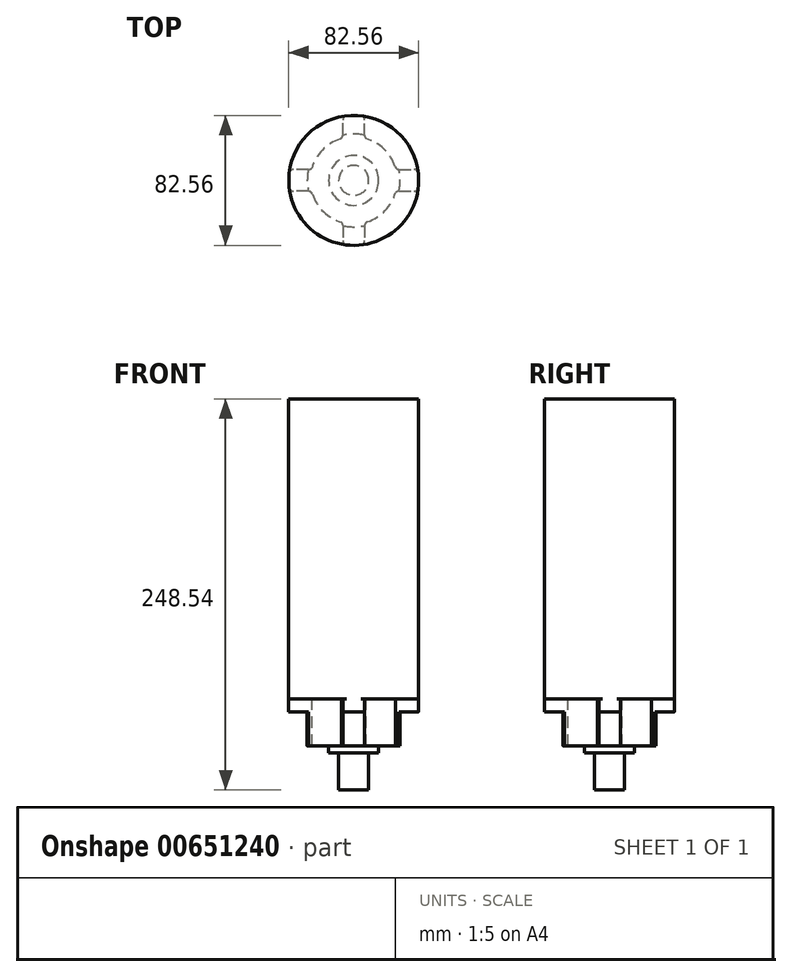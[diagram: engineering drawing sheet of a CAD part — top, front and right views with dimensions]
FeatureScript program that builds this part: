
annotation { "Feature Type Name" : "Feature", "Feature Type Description" : "" }
export const myFeature = defineFeature(function(context is Context, id is Id, definition is map)
    precondition{}
    {
        {
            var Q0;
            Q0=qCreatedBy(makeId("Top.planeOp"),FACE);
            var sketch = newSketch(context, id + "F0", { "sketchPlane" : qUnion([Q0])});
            skCircle(sketch, "E0", {"center": v(0, 0) * mm, "radius": 41.28 * mm});
            skSolve(sketch);
        }
        {
            var Q0;
            Q0=makeQuery(id+"F0.imprint","IMPRINT",FACE,{"disambiguationData":[TD([[makeQuery(id+"F0.imprint","IMPRINT",EDGE,{"derivedFrom":sQuery(id+"F0.wireOp",EDGE,"E0")}),1.0]])]});
            extrude(context, id + "F1", {"entities" : qUnion([Q0]), "depth" : 190.5 * mm, "offsetDistance" : 25.4 * mm});
        }
        {
            var Q0;
            Q0=makeQuery(id+"F1.opExtrude","CAP_FACE",FACE,{"disambiguationData":[OSD([sQuery(id+"F0.wireOp",EDGE,"E0")])],"isStart":true});
            var sketch = newSketch(context, id + "F2", { "sketchPlane" : qUnion([Q0])});
            skLineSegment(sketch, "E1", {"start": v(0, 0) * mm, "end": v(0, 8.34) * mm});
            skLineSegment(sketch, "E2", {"start": v(0, 0) * mm, "end": v(6.98, 0) * mm});
            skLineSegment(sketch, "E3", {"start": v(6.91, 28.9) * mm, "end": v(6.91, 38.32) * mm});
            skLineSegment(sketch, "E4.MirrorCS", {"start": v(-6.91, 28.68) * mm, "end": v(-6.91, 38.32) * mm});
            skLineSegment(sketch, "E5.MirrorCS", {"start": v(-6.91, 28.68) * mm, "end": v(-6.91, 28.65) * mm});
            skArc(sketch, "E6", {"start": v(-11.65, 39.6) * mm, "mid": v(-0.46, -41.27) * mm, "end": v(12.53, 39.33) * mm});
            skArc(sketch, "E7", {"start": v(4.48, 41.03) * mm, "mid": v(0, 41.27) * mm, "end": v(-4.48, 41.03) * mm});
            skPoint(sketch, "E8.newPointB", {"position": v(6.91, 40.69) * mm});
            skArc(sketch, "E8.filletArc", {"start": v(6.91, 38.32) * mm, "mid": v(6.22, 40.14) * mm, "end": v(4.48, 41.03) * mm});
            skPoint(sketch, "E9.newPointB", {"position": v(-6.91, 40.69) * mm});
            skArc(sketch, "E9.filletArc", {"start": v(-4.48, 41.03) * mm, "mid": v(-6.22, 40.14) * mm, "end": v(-6.91, 38.32) * mm});
            skPoint(sketch, "E10.newPointA", {"position": v(6.91, 28.65) * mm});
            skArc(sketch, "E10.filletArc", {"start": v(6.91, 28.9) * mm, "mid": v(7.43, 27.3) * mm, "end": v(8.8, 26.3) * mm});
            skPoint(sketch, "E11.MirrorP", {"position": v(-6.91, 28.65) * mm});
            skArc(sketch, "E12.MirrorCS", {"start": v(-6.91, 28.68) * mm, "mid": v(-7.17, 27.52) * mm, "end": v(-7.9, 26.57) * mm});
            skLineSegment(sketch, "E13.1.0", {"start": v(-28.68, -6.91) * mm, "end": v(-38.32, -6.91) * mm});
            skArc(sketch, "E13.1.1", {"start": v(-41.03, -4.48) * mm, "mid": v(-40.14, -6.22) * mm, "end": v(-38.32, -6.91) * mm});
            skArc(sketch, "E13.1.2", {"start": v(-38.32, 6.91) * mm, "mid": v(-40.14, 6.22) * mm, "end": v(-41.03, 4.48) * mm});
            skLineSegment(sketch, "E13.1.3", {"start": v(-28.9, 6.91) * mm, "end": v(-38.32, 6.91) * mm});
            skArc(sketch, "E13.1.4", {"start": v(-28.9, 6.91) * mm, "mid": v(-27.3, 7.43) * mm, "end": v(-26.3, 8.8) * mm});
            skArc(sketch, "E13.1.5", {"start": v(-28.68, -6.91) * mm, "mid": v(-27.52, -7.17) * mm, "end": v(-26.57, -7.9) * mm});
            skLineSegment(sketch, "E13.2.0", {"start": v(6.91, -28.68) * mm, "end": v(6.91, -38.32) * mm});
            skArc(sketch, "E13.2.1", {"start": v(4.48, -41.03) * mm, "mid": v(6.22, -40.14) * mm, "end": v(6.91, -38.32) * mm});
            skArc(sketch, "E13.2.2", {"start": v(-6.91, -38.32) * mm, "mid": v(-6.22, -40.14) * mm, "end": v(-4.48, -41.03) * mm});
            skLineSegment(sketch, "E13.2.3", {"start": v(-6.91, -28.9) * mm, "end": v(-6.91, -38.32) * mm});
            skArc(sketch, "E13.2.4", {"start": v(-6.91, -28.9) * mm, "mid": v(-7.43, -27.3) * mm, "end": v(-8.8, -26.3) * mm});
            skArc(sketch, "E13.2.5", {"start": v(6.91, -28.68) * mm, "mid": v(7.17, -27.52) * mm, "end": v(7.9, -26.57) * mm});
            skLineSegment(sketch, "E13.3.0", {"start": v(28.68, 6.91) * mm, "end": v(38.32, 6.91) * mm});
            skArc(sketch, "E13.3.1", {"start": v(41.03, 4.48) * mm, "mid": v(40.14, 6.22) * mm, "end": v(38.32, 6.91) * mm});
            skArc(sketch, "E13.3.2", {"start": v(38.32, -6.91) * mm, "mid": v(40.14, -6.22) * mm, "end": v(41.03, -4.48) * mm});
            skLineSegment(sketch, "E13.3.3", {"start": v(28.9, -6.91) * mm, "end": v(38.32, -6.91) * mm});
            skArc(sketch, "E13.3.4", {"start": v(28.9, -6.91) * mm, "mid": v(27.3, -7.43) * mm, "end": v(26.3, -8.8) * mm});
            skArc(sketch, "E13.3.5", {"start": v(28.68, 6.91) * mm, "mid": v(27.52, 7.17) * mm, "end": v(26.57, 7.9) * mm});
            skArc(sketch, "E14", {"start": v(-26.57, -7.9) * mm, "mid": v(-19.93, -19.27) * mm, "end": v(-8.8, -26.3) * mm});
            skArc(sketch, "E15.1.0", {"start": v(7.9, -26.57) * mm, "mid": v(19.27, -19.93) * mm, "end": v(26.3, -8.8) * mm});
            skArc(sketch, "E15.2.0", {"start": v(26.57, 7.9) * mm, "mid": v(19.93, 19.27) * mm, "end": v(8.8, 26.3) * mm});
            skArc(sketch, "E16.3.3.0", {"start": v(-7.9, 26.57) * mm, "mid": v(-19.27, 19.93) * mm, "end": v(-26.3, 8.8) * mm});
            skSolve(sketch);
        }
        {
            var Q0;
            Q0=makeQuery(id+"F2.imprint","IMPRINT",FACE,{"disambiguationData":[TD([[makeQuery(id+"F2.imprint","IMPRINT",EDGE,{"derivedFrom":sQuery(id+"F2.wireOp",EDGE,"E3")}),1.0]])]});
            extrude(context, id + "F3", {"entities" : qUnion([Q0]), "operationType" : NewBodyOperationType.ADD, "depth" : 8.25 * mm, "offsetDistance" : 25.4 * mm});
        }
        {
            var Q0;
            Q0=makeQuery(id+"F3.opExtrude","CAP_FACE",FACE,{"disambiguationData":[OSD([sQuery(id+"F2.wireOp",EDGE,"E3"),sQuery(id+"F2.wireOp",EDGE,"E4.MirrorCS"),sQuery(id+"F2.wireOp",EDGE,"E6"),sQuery(id+"F2.wireOp",EDGE,"E7"),sQuery(id+"F2.wireOp",EDGE,"E8.filletArc"),sQuery(id+"F2.wireOp",EDGE,"E9.filletArc"),sQuery(id+"F2.wireOp",EDGE,"E10.filletArc"),sQuery(id+"F2.wireOp",EDGE,"E12.MirrorCS"),sQuery(id+"F2.wireOp",EDGE,"E13.1.0"),sQuery(id+"F2.wireOp",EDGE,"E13.1.1"),sQuery(id+"F2.wireOp",EDGE,"E13.1.2"),sQuery(id+"F2.wireOp",EDGE,"E13.1.3"),sQuery(id+"F2.wireOp",EDGE,"E13.1.4"),sQuery(id+"F2.wireOp",EDGE,"E13.1.5"),sQuery(id+"F2.wireOp",EDGE,"E13.2.0"),sQuery(id+"F2.wireOp",EDGE,"E13.2.1"),sQuery(id+"F2.wireOp",EDGE,"E13.2.2"),sQuery(id+"F2.wireOp",EDGE,"E13.2.3"),sQuery(id+"F2.wireOp",EDGE,"E13.2.4"),sQuery(id+"F2.wireOp",EDGE,"E13.2.5"),sQuery(id+"F2.wireOp",EDGE,"E13.3.0"),sQuery(id+"F2.wireOp",EDGE,"E13.3.1"),sQuery(id+"F2.wireOp",EDGE,"E13.3.2"),sQuery(id+"F2.wireOp",EDGE,"E13.3.3"),sQuery(id+"F2.wireOp",EDGE,"E13.3.4"),sQuery(id+"F2.wireOp",EDGE,"E13.3.5"),sQuery(id+"F2.wireOp",EDGE,"E14"),sQuery(id+"F2.wireOp",EDGE,"E15.1.0"),sQuery(id+"F2.wireOp",EDGE,"E15.2.0"),sQuery(id+"F2.wireOp",EDGE,"E16.3.3.0")])],"isStart":false});
            var sketch = newSketch(context, id + "F4", { "sketchPlane" : qUnion([Q0])});
            skCircle(sketch, "E17", {"center": v(0, 0) * mm, "radius": 29.53 * mm});
            skSolve(sketch);
        }
        {
            var Q0;
            Q0=makeQuery(id+"F4.imprint","IMPRINT",FACE,{"disambiguationData":[TD([[makeQuery(id+"F4.imprint","IMPRINT",EDGE,{"derivedFrom":sQuery(id+"F4.wireOp",EDGE,"E17")}),1.0]])]});
            extrude(context, id + "F5", {"entities" : qUnion([Q0]), "operationType" : NewBodyOperationType.ADD, "depth" : 21.84 * mm, "offsetDistance" : 25.4 * mm});
        }
        {
            var Q0;
            Q0=makeQuery(id+"F5.opExtrude","CAP_FACE",FACE,{"disambiguationData":[OSD([sQuery(id+"F4.wireOp",EDGE,"E17")])],"isStart":false});
            var sketch = newSketch(context, id + "F6", { "sketchPlane" : qUnion([Q0])});
            skCircle(sketch, "E18", {"center": v(0, 0) * mm, "radius": 15.88 * mm});
            skSolve(sketch);
        }
        {
            var Q0;
            Q0=makeQuery(id+"F6.imprint","IMPRINT",FACE,{"disambiguationData":[TD([[makeQuery(id+"F6.imprint","IMPRINT",EDGE,{"derivedFrom":sQuery(id+"F6.wireOp",EDGE,"E18")}),1.0]])]});
            extrude(context, id + "F7", {"entities" : qUnion([Q0]), "operationType" : NewBodyOperationType.ADD, "depth" : 4.2 * mm, "offsetDistance" : 25.4 * mm});
        }
        {
            var Q0;
            Q0=makeQuery(id+"F7.opExtrude","CAP_FACE",FACE,{"disambiguationData":[OSD([sQuery(id+"F6.wireOp",EDGE,"E18")])],"isStart":false});
            var sketch = newSketch(context, id + "F8", { "sketchPlane" : qUnion([Q0])});
            skCircle(sketch, "E19", {"center": v(0, 0) * mm, "radius": 9.53 * mm});
            skSolve(sketch);
        }
        {
            var Q0;
            Q0=makeQuery(id+"F8.imprint","IMPRINT",FACE,{"disambiguationData":[TD([[makeQuery(id+"F8.imprint","IMPRINT",EDGE,{"derivedFrom":sQuery(id+"F8.wireOp",EDGE,"E19")}),1.0]])]});
            extrude(context, id + "F9", {"entities" : qUnion([Q0]), "operationType" : NewBodyOperationType.ADD, "depth" : 23.75 * mm, "offsetDistance" : 25.4 * mm});
        }
    });
